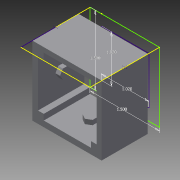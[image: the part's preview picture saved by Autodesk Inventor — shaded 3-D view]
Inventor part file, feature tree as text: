
AUTODESK INVENTOR PART (.ipt)
format: ipt  version: 2013 SP2 (Build 170200200, 200)  size: 190,976 bytes
history: native  units: in
note: dims shown in document units (in); Inventor stores cm internally (conversion verified against a paired STEP export)
features: sketch x9, extrude x8
ambient origin geometry x8: Origin, YZ Plane, XZ Plane, XY Plane, X Axis, Y Axis, Z Axis, Center Point
bodies: Solid1 (feature_tree)
feature tree (17):
  sketch  "Sketch1"  dims[d0=1.02in d1=1.02in]
  extrude  "Extrusion1"  Depth=1.02in
  sketch  "Sketch2"  dims[d4=1.5in d5=1.5in]
  sketch  "Sketch3"  dims[d6=1.5in d7=0.0in d8=0.125in]
  extrude  "Extrusion2"  Depth=1.5in
  extrude  "Extrusion3"  Depth=0.125in
  extrude  "Extrusion4"  Depth=0.125in
  extrude  "Extrusion5"  Depth=1.5in TaperAngle=0.0deg
  extrude  "Extrusion6"  Depth=0.1in TaperAngle=0.0deg
  extrude  "Extrusion7"  Depth=0.75in
  extrude  "Extrusion8"  Depth=0.123in
  sketch  "Sketch4"  dims[d9=0.125in d10=0.125in]
  sketch  "Sketch5"  dims[d11=0.125in d12=1.5in d13=0.0in]
  sketch  "Sketch6"  dims[d14=0.75in d17=0.1in d18=0.0in]
  sketch  "Sketch7"  dims[d19=0.51in d20=0.75in]
  sketch  "Sketch8"  dims[d22=0.123in d23=0.123in]
  sketch  "Sketch9"  dims[d24=0.1in d25=0.0in d26=0.75in d27=0.51in d28=0.123in d29=0.1in d30=0.0in d31=0.75in d32=0.51in d33=0.123in d34=0.1in d35=0.0in d36=0.25in d37=0.0in d38=0.25in d39=0.0in]
